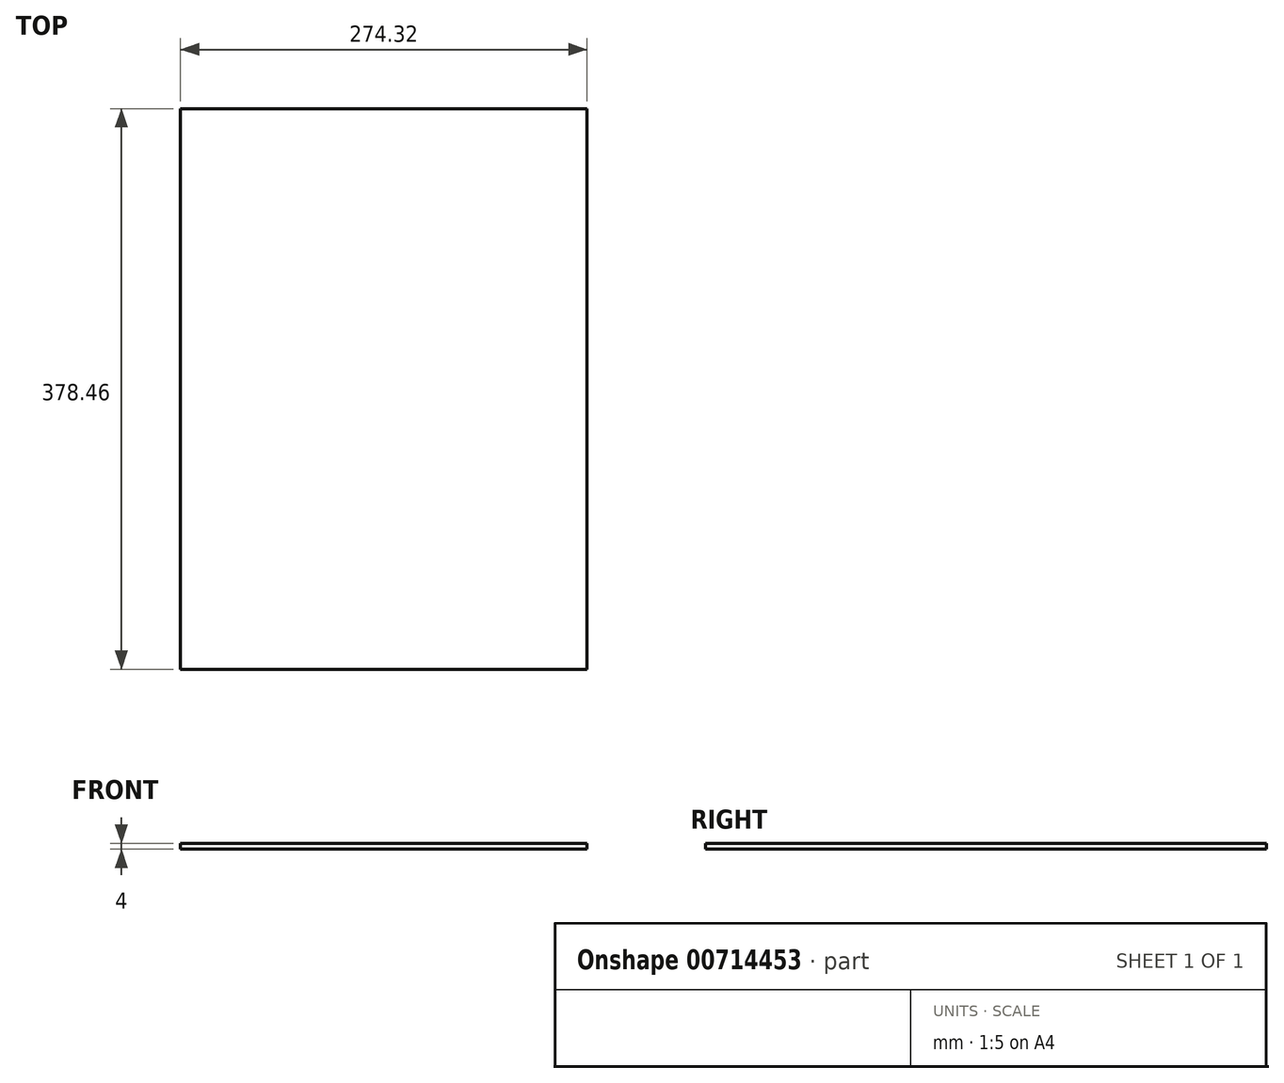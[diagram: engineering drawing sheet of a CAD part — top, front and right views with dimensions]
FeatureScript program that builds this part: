
annotation { "Feature Type Name" : "Feature", "Feature Type Description" : "" }
export const myFeature = defineFeature(function(context is Context, id is Id, definition is map)
    precondition{}
    {
        {
            var Q0;
            Q0=qCreatedBy(makeId("Top.planeOp"),FACE);
            var sketch = newSketch(context, id + "F0", { "sketchPlane" : qUnion([Q0])});
            skLineSegment(sketch, "E0.bottom", {"start": v(-137.16, 189.23) * mm, "end": v(137.16, 189.23) * mm});
            skLineSegment(sketch, "E0.top", {"start": v(-137.16, -189.23) * mm, "end": v(137.16, -189.23) * mm});
            skLineSegment(sketch, "E0.left", {"start": v(-137.16, 189.23) * mm, "end": v(-137.16, -189.23) * mm});
            skLineSegment(sketch, "E0.right", {"start": v(137.16, 189.23) * mm, "end": v(137.16, -189.23) * mm});
            skPoint(sketch, "E0.middle", {"position": v(0, 0) * mm});
            skSolve(sketch);
        }
        {
            var Q0;
            Q0 = qSketchRegion(id + "F0", true);
            extrude(context, id + "F1", {"entities" : qUnion([Q0]), "depth" : 4 * mm, "offsetDistance" : 25.4 * mm});
        }
    });
